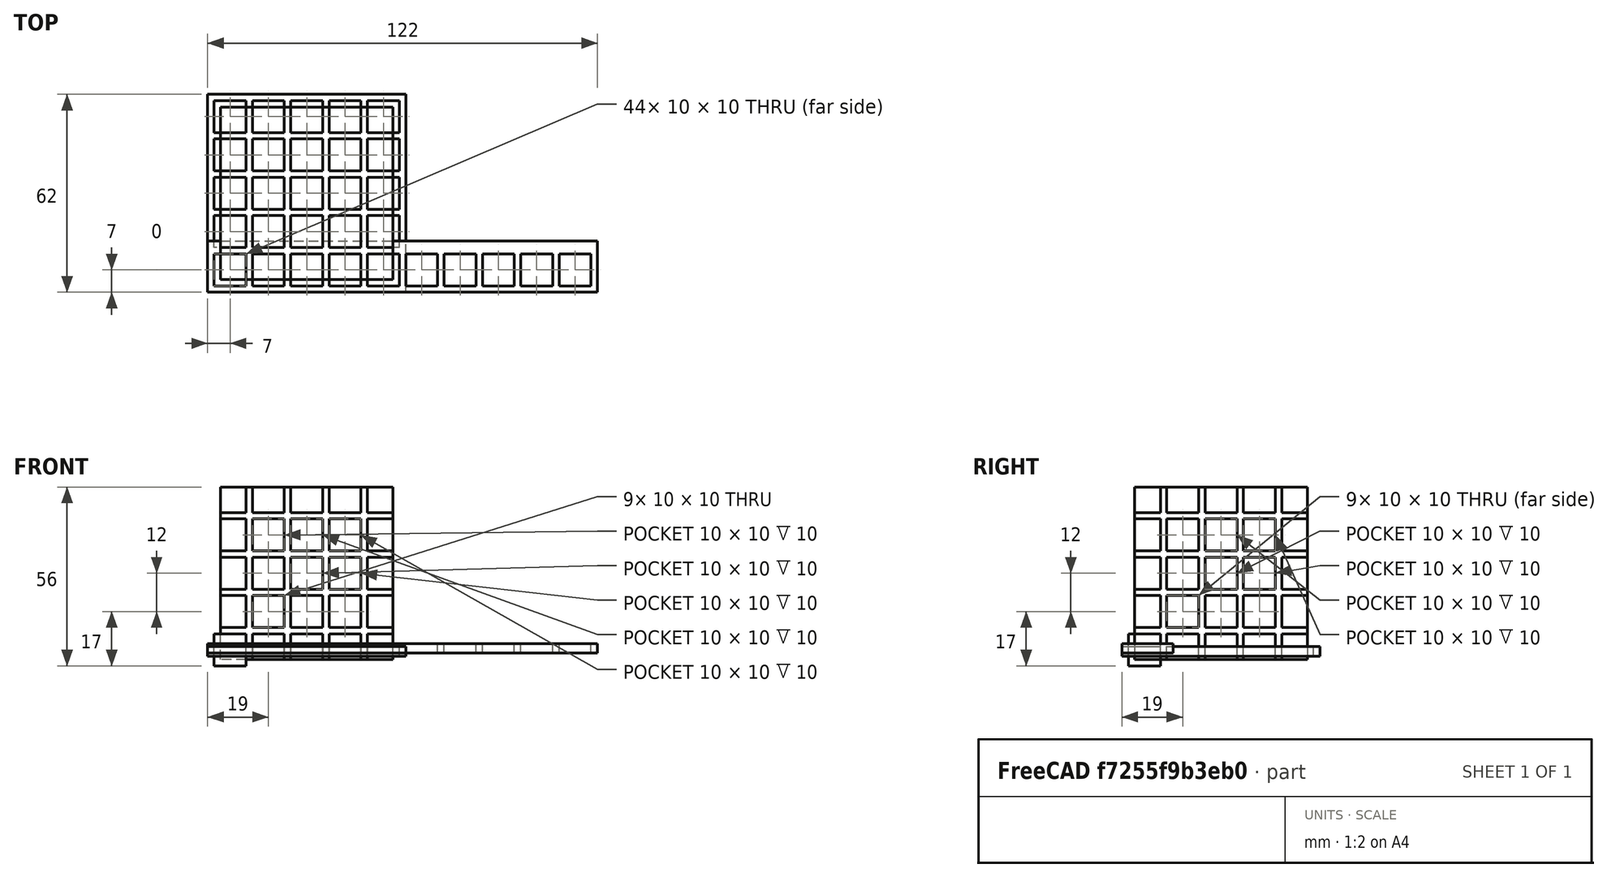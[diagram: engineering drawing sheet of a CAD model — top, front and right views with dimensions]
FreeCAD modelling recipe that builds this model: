
FCSTD DOCUMENT  (FreeCAD 0.21R33694 (Git))
Label: OJT1_T10P01_repeticion
License: All rights reserved
LicenseURL: http://en.wikipedia.org/wiki/All_rights_reserved
objects: Part::Box×6, Part::FeaturePython×3, Part::Cut×3
note: 9 computed .brp shape members not serialized (recipe doc carries the construction recipe); baked Part::Feature solids carry a one-line shape summary decoded from their .brp

FEATURE [Part::Box] Box  label="Cube"
  AttacherType = Attacher::AttachEngine3D
  Height = 10
  Length = 10
  Width = 10
FEATURE [Part::FeaturePython] Array  # Draft array (typed FeaturePython)
  AlwaysSyncPlacement = false
  Angle = 360
  ArrayType = 0
  Axis = (0,0,1)
  Base = -> Box
  Center = (0,0,0)
  Count = 10
  ExpandArray = false
  Fuse = false
  IntervalAxis = (0,0,0)
  IntervalX = (12,0,0)
  IntervalY = (0,100,0)
  IntervalZ = (0,0,100)
  NumberCircles = 3
  NumberPolar = 5
  NumberX = 10
  NumberY = 1
  NumberZ = 1
  PlacementList = 10 placements: arithmetic series from (0,0,0) step (12,0,0) to (108,0,0)
  RadialDistance = 50
  ScaleList = (10) [(1,1,1),(1,1,1),(1,1,1),(1,1,1),(1,1,1),(1,1,1),(1,1,1),(1,1,1),(1,1,1),(1,1,1)]
  Symmetry = 1
  TangentialDistance = 25
FEATURE [Part::Box] Box001  label="Cube001"
  AttacherType = Attacher::AttachEngine3D
  Height = 3
  Length = 122
  Placement = pos=(-2,-2,4) rot=(0,0,1;0rad)
  Width = 16
FEATURE [Part::Cut] Cut
  Base = -> Box001
  Refine = true
  Tool = -> Array
FEATURE [Part::Box] Box002  label="Cube002"
  AttacherType = Attacher::AttachEngine3D
  Height = 10
  Length = 10
  Width = 10
FEATURE [Part::FeaturePython] Array001  # Draft array (typed FeaturePython)
  AlwaysSyncPlacement = false
  Angle = 360
  ArrayType = 0
  Axis = (0,0,1)
  Base = -> Box002
  Center = (0,0,0)
  Count = 25
  ExpandArray = false
  Fuse = false
  IntervalAxis = (0,0,0)
  IntervalX = (12,0,0)
  IntervalY = (0,12,0)
  IntervalZ = (0,0,100)
  NumberCircles = 3
  NumberPolar = 5
  NumberX = 5
  NumberY = 5
  NumberZ = 1
  PlacementList = 25 placements: [(0,0,0),(0,12,0),(0,24,0),(0,36,0),(0,48,0),(12,0,0),(12,12,0),(12,24,0),(12,36,0),(12,48,0),(24,0,0),(24,12,0),(24,24,0),(24,36,0),(24,48,0),(36,0,0),(36,12,0),(36,24,0),(36,36,0),(36,48,0),(48,0,0),(48,12,0),(48,24,0),(48,36,0),(48,48,0)]
  RadialDistance = 50
  ScaleList = (25) [(1,1,1),(1,1,1),(1,1,1),(1,1,1),(1,1,1),(1,1,1),(1,1,1),(1,1,1),(1,1,1),(1,1,1),(1,1,1),(1,1,1),(1,1,1),(1,1,1),(1,1,1),(1,1,1),(1,1,1),(1,1,1),+7 more]
  Symmetry = 1
  TangentialDistance = 25
FEATURE [Part::Box] Box003  label="Cube003"
  AttacherType = Attacher::AttachEngine3D
  Height = 3
  Length = 62
  Placement = pos=(-2,-2,3) rot=(0,0,1;0rad)
  Width = 62
FEATURE [Part::Cut] Cut001
  Base = -> Box003
  Refine = true
  Tool = -> Array001
FEATURE [Part::Box] Box004  label="Cube004"
  AttacherType = Attacher::AttachEngine3D
  Height = 10
  Length = 10
  Width = 10
FEATURE [Part::FeaturePython] Array002  # Draft array (typed FeaturePython)
  AlwaysSyncPlacement = false
  Angle = 360
  ArrayType = 0
  Axis = (0,0,1)
  Base = -> Box004
  Center = (0,0,0)
  Count = 125
  ExpandArray = false
  Fuse = false
  IntervalAxis = (0,0,0)
  IntervalX = (12,0,0)
  IntervalY = (0,12,0)
  IntervalZ = (0,0,12)
  NumberCircles = 3
  NumberPolar = 5
  NumberX = 5
  NumberY = 5
  NumberZ = 5
  PlacementList = 125 placements: [(0,0,0),(0,0,12),(0,0,24),(0,0,36),(0,0,48),(0,12,0),(0,12,12),(0,12,24),(0,12,36),(0,12,48),(0,24,0),(0,24,12),(0,24,24),(0,24,36),(0,24,48),(0,36,0),(0,36,12),(0,36,24),(0,36,36),(0,36,48),(0,48,0),(0,48,12),(0,48,24),(0,48,36),(0,48,48),(12,0,0),(12,0,12),(12,0,24),(12,0,36),(12,0,48),(12,12,0),(12,12,12),(12,12,24),(12,12,36),(12,12,48),(12,24,0),(12,24,12),(12,24,24),(12,24,36),(12,24,48),+85 more]
  RadialDistance = 50
  ScaleList = (125) [(1,1,1),(1,1,1),(1,1,1),(1,1,1),(1,1,1),(1,1,1),(1,1,1),(1,1,1),(1,1,1),(1,1,1),(1,1,1),(1,1,1),(1,1,1),(1,1,1),(1,1,1),(1,1,1),(1,1,1),(1,1,1),+107 more]
  Symmetry = 1
  TangentialDistance = 25
FEATURE [Part::Box] Box005  label="Cube005"
  AttacherType = Attacher::AttachEngine3D
  Height = 54
  Length = 54
  Placement = pos=(2,2,2) rot=(0,0,1;0rad)
  Width = 54
FEATURE [Part::Cut] Cut002
  Base = -> Box005
  Refine = true
  Tool = -> Array002
